# Revit family: Lighting_Linear_LED_StarTek_Micro-Optimo-Direct-Rotational-Mount
name_source: partatom
category: Lighting Fixtures
units: mm (PartAtom-declared; Revit-internal decimal feet)

## family parameters
Cut with Voids When Loaded = No
Host = Face
Light Source = No
OmniClass Number = 23.80.70.11
OmniClass Title = Luminaries for Internal Lighting
Part Type = Normal
Room Calculation Point = No
Round Connector Dimension = Use Diameter
Shared = No

## types (1)
- Not a Type - Load Type Catalog!
    Apparent Load = 0 VA
    Assembly Code = D5020200
    CRI = 80
    Default Elevation = 48 "
    Description = Micro Optimo Direct
    Distribution = SD
    Edition number = 1
    Electrical Disconnect = Yes
    Frequency = 0 Hz
    Height = 2 "
    Input Wattage = 0 W
    Keynote = 16500
    Lamp = LED
    Lamp length 4' = Yes
    Lamp length 8' = No
    Length = 48 "
    Manufacturer = StarTek Lighting
    Number of Poles = 1
    Phase = 1
    Photometric Note = Import IES files https://starteklightingamerica.com
    Photometric Option = Light-Source_StarTek_Micro-Optimo-Direct-Rotational-Mount : Not a Type - Load Type Catalog!
    Photometric Web File Note = Please remember to reload the shared light file with the type catalog for all available light options and link the proper .ies file to the shared file.
    Power Factor = 1
    Product Guid = 2d1d840d-481b-43d5-8dc0-894fcfffd1a4
    Product data url = https://www.bimobject.com
    Type Comments = Linear Lighting Fixture
    URL = https://starteklightingamerica.com
    Voltage = 120 V
    Weight = 0.00 lbf
    Width = 2 "
    z_Wall Mount = Montage : Rotational Wall Mount (RWM)

## geometry (parser evidence)
native form markers: Sweep x11
no freeform markers — native parametric forms only
